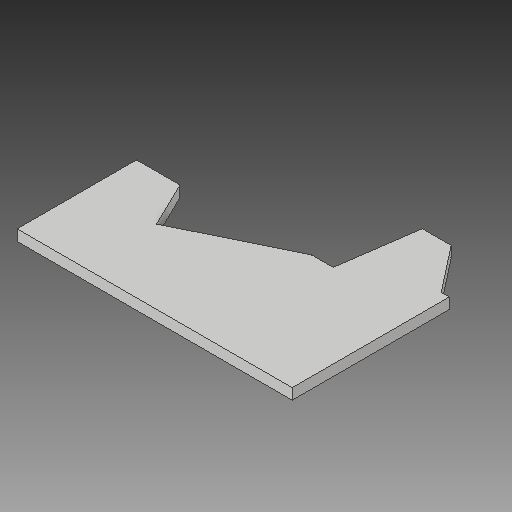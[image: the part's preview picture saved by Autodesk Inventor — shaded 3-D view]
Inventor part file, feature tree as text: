
AUTODESK INVENTOR PART (.ipt)
format: ipt  version: 2017 (Build 210142000, 142)  size: 111,616 bytes
history: native  units: in
note: dims shown in document units (in); Inventor stores cm internally (conversion verified against a paired STEP export)
features: extrude x1
ambient origin geometry x8: Origin, YZ Plane, XZ Plane, XY Plane, X Axis, Y Axis, Z Axis, Center Point
bodies: Solid1 (feature_tree)
feature tree (1):
  extrude  "Extrusion1"  Depth=0.75in TaperAngle=0.0deg
